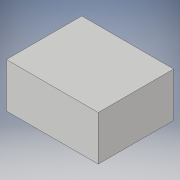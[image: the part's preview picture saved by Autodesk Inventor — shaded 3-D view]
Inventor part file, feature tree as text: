
AUTODESK INVENTOR PART (.ipt)
format: ipt  version: 2019.3 (Build 233278000, 278)  size: 86,016 bytes
history: native  units: mm
features: extrude x1, sketch x1
ambient origin geometry x8: Origin, YZ Plane, XZ Plane, XY Plane, X Axis, Y Axis, Z Axis, Center Point
bodies: Solid1 (feature_tree)
feature tree (2):
  extrude  "Extrusion1"  Depth=24.5mm
  sketch  "Sketch1"  dims[d0=29.854mm d1=24.5mm d2=14.5mm d3=0.0mm]
